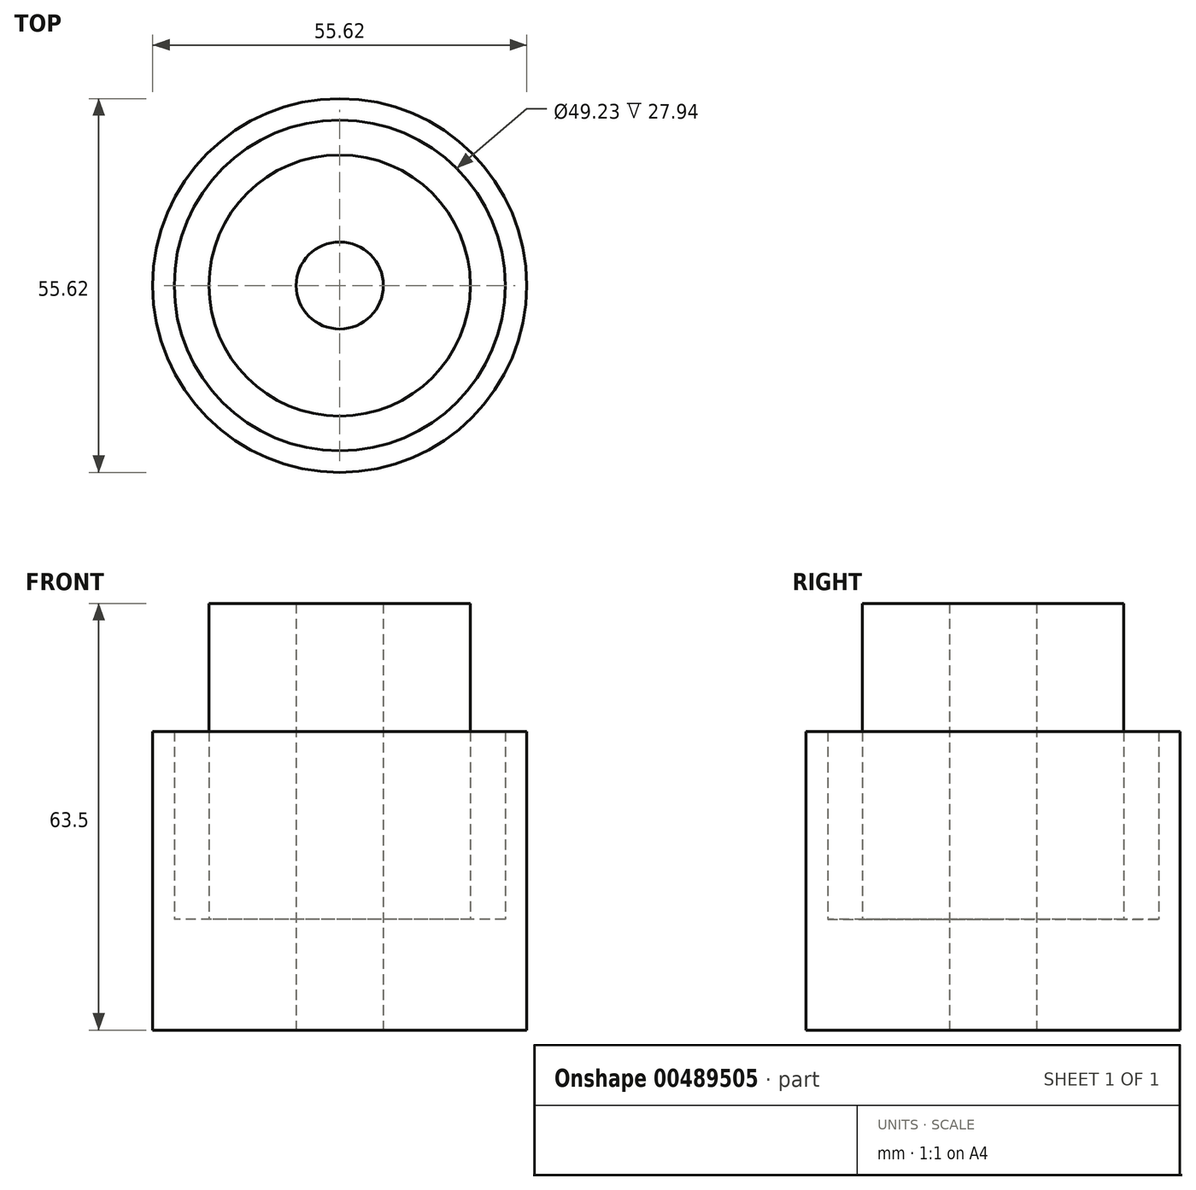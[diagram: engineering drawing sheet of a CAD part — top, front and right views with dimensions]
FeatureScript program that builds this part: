
annotation { "Feature Type Name" : "Feature", "Feature Type Description" : "" }
export const myFeature = defineFeature(function(context is Context, id is Id, definition is map)
    precondition{}
    {
        {
            var Q0;
            Q0=qCreatedBy(makeId("Top.planeOp"),FACE);
            var sketch = newSketch(context, id + "F0", { "sketchPlane" : qUnion([Q0])});
            skCircle(sketch, "E0", {"center": v(0, 0) * mm, "radius": 19.43 * mm});
            skCircle(sketch, "E1", {"center": v(0, 0) * mm, "radius": 24.61 * mm});
            skPoint(sketch, "E2.start.orphan", {"position": v(0, 19.43) * mm});
            skCircle(sketch, "E3", {"center": v(0, 0) * mm, "radius": 27.81 * mm});
            skCircle(sketch, "E4", {"center": v(0, 0) * mm, "radius": 6.48 * mm});
            skSolve(sketch);
        }
        {
            var Q0;
            Q0=makeQuery(id+"F0.imprint","IMPRINT",FACE,{"disambiguationData":[TD([[makeQuery(id+"F0.imprint","IMPRINT",EDGE,{"derivedFrom":sQuery(id+"F0.wireOp",EDGE,"E1")}),-1.0]])]});
            var Q1;
            Q1=makeQuery(id+"F0.imprint","IMPRINT",FACE,{"disambiguationData":[TD([[makeQuery(id+"F0.imprint","IMPRINT",EDGE,{"derivedFrom":sQuery(id+"F0.wireOp",EDGE,"E0")}),1.0]])]});
            extrude(context, id + "F1", {"entities" : qUnion([Q0, Q1]), "depth" : 27.94 * mm, "offsetDistance" : 25.4 * mm});
        }
        {
            var Q0;
            Q0=makeQuery(id+"F0.imprint","IMPRINT",FACE,{"disambiguationData":[TD([[makeQuery(id+"F0.imprint","IMPRINT",EDGE,{"derivedFrom":sQuery(id+"F0.wireOp",EDGE,"E0")}),1.0]])]});
            var Q1;
            Q1=makeQuery(id+"F0.imprint","IMPRINT",FACE,{"disambiguationData":[TD([[makeQuery(id+"F0.imprint","IMPRINT",EDGE,{"derivedFrom":sQuery(id+"F0.wireOp",EDGE,"E0")}),-1.0]])]});
            var Q2;
            Q2=makeQuery(id+"F0.imprint","IMPRINT",FACE,{"disambiguationData":[TD([[makeQuery(id+"F0.imprint","IMPRINT",EDGE,{"derivedFrom":sQuery(id+"F0.wireOp",EDGE,"E1")}),-1.0]])]});
            extrude(context, id + "F2", {"entities" : qUnion([Q0, Q1, Q2]), "operationType" : NewBodyOperationType.ADD, "oppositeDirection" : true, "depth" : 16.5 * mm, "offsetDistance" : 25.4 * mm});
        }
        {
            var Q0;
            Q0=makeQuery(id+"F1.opExtrude","CAP_FACE",FACE,{"disambiguationData":[OSD([sQuery(id+"F0.wireOp",EDGE,"E0"),sQuery(id+"F0.wireOp",EDGE,"E4")])],"isStart":false});
            extrude(context, id + "F3", {"entities" : qUnion([Q0]), "operationType" : NewBodyOperationType.ADD, "depth" : 19.05 * mm, "offsetDistance" : 25.4 * mm});
        }
    });
